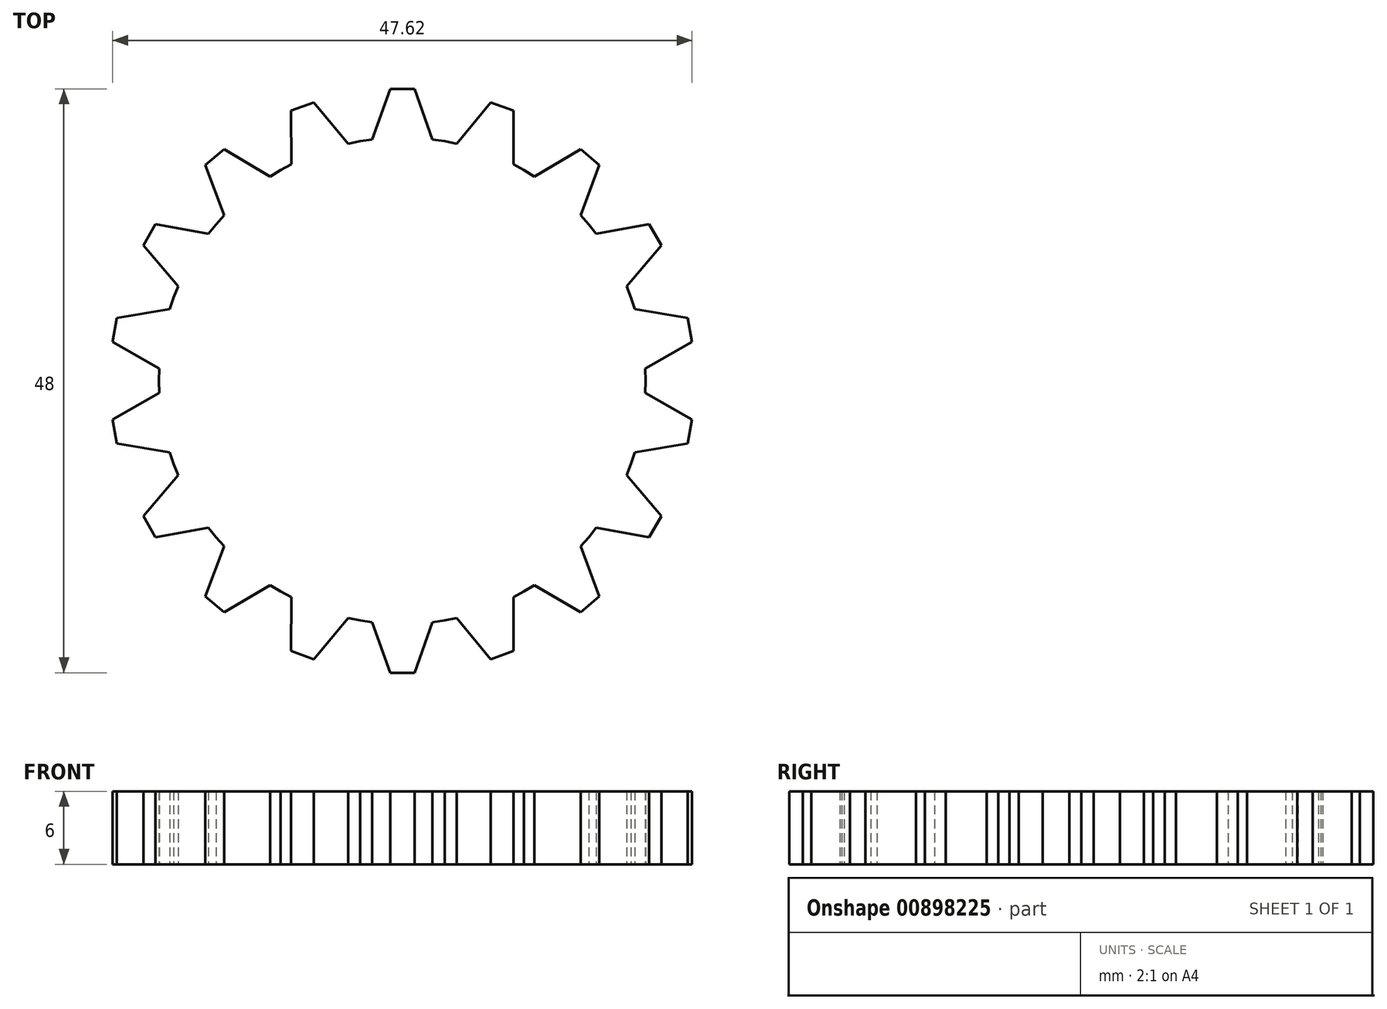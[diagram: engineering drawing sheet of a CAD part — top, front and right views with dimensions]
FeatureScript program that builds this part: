
annotation { "Feature Type Name" : "Feature", "Feature Type Description" : "" }
export const myFeature = defineFeature(function(context is Context, id is Id, definition is map)
    precondition{}
    {
        {
            var Q0;
            Q0=qCreatedBy(makeId("Top.planeOp"),FACE);
            var sketch = newSketch(context, id + "F0", { "sketchPlane" : qUnion([Q0])});
            skCircle(sketch, "E0", {"center": v(0, 0) * mm, "radius": 20 * mm});
            skLineSegment(sketch, "E1", {"start": v(0, 0) * mm, "end": v(-6.59, 37.35) * mm});
            skLineSegment(sketch, "E2", {"start": v(0, 24) * mm, "end": v(-1, 24) * mm});
            skLineSegment(sketch, "E3", {"start": v(-1, 24) * mm, "end": v(-2.48, 19.85) * mm});
            skLineSegment(sketch, "E4", {"start": v(-2.48, 19.85) * mm, "end": v(-3.47, 19.7) * mm});
            skLineSegment(sketch, "E5.MirrorCS", {"start": v(0, 24) * mm, "end": v(1, 24) * mm});
            skLineSegment(sketch, "E6.MirrorCS", {"start": v(2.48, 19.85) * mm, "end": v(3.47, 19.7) * mm});
            skLineSegment(sketch, "E7.MirrorCS", {"start": v(1, 24) * mm, "end": v(2.48, 19.85) * mm});
            skLineSegment(sketch, "E8.1.0", {"start": v(-7.27, 22.9) * mm, "end": v(-4.45, 19.5) * mm});
            skLineSegment(sketch, "E8.1.1", {"start": v(-9.15, 22.21) * mm, "end": v(-9.12, 17.8) * mm});
            skLineSegment(sketch, "E8.1.2", {"start": v(-8.2, 22.55) * mm, "end": v(-7.27, 22.9) * mm});
            skLineSegment(sketch, "E8.1.3", {"start": v(-4.45, 19.5) * mm, "end": v(-3.47, 19.7) * mm});
            skLineSegment(sketch, "E8.1.4", {"start": v(-8.2, 22.55) * mm, "end": v(-9.15, 22.21) * mm});
            skLineSegment(sketch, "E8.1.5", {"start": v(-9.12, 17.8) * mm, "end": v(-10, 17.32) * mm});
            skLineSegment(sketch, "E8.2.0", {"start": v(-14.66, 19.03) * mm, "end": v(-10.85, 16.8) * mm});
            skLineSegment(sketch, "E8.2.1", {"start": v(-16.2, 17.74) * mm, "end": v(-14.66, 13.6) * mm});
            skLineSegment(sketch, "E8.2.2", {"start": v(-15.43, 18.39) * mm, "end": v(-14.66, 19.03) * mm});
            skLineSegment(sketch, "E8.2.3", {"start": v(-10.85, 16.8) * mm, "end": v(-10, 17.32) * mm});
            skLineSegment(sketch, "E8.2.4", {"start": v(-15.43, 18.39) * mm, "end": v(-16.2, 17.74) * mm});
            skLineSegment(sketch, "E8.2.5", {"start": v(-14.66, 13.6) * mm, "end": v(-15.32, 12.86) * mm});
            skLineSegment(sketch, "E8.3.0", {"start": v(-20.28, 12.87) * mm, "end": v(-15.94, 12.07) * mm});
            skLineSegment(sketch, "E8.3.1", {"start": v(-21.28, 11.13) * mm, "end": v(-18.43, 7.77) * mm});
            skLineSegment(sketch, "E8.3.2", {"start": v(-20.78, 12) * mm, "end": v(-20.28, 12.87) * mm});
            skLineSegment(sketch, "E8.3.3", {"start": v(-15.94, 12.07) * mm, "end": v(-15.32, 12.86) * mm});
            skLineSegment(sketch, "E8.3.4", {"start": v(-20.78, 12) * mm, "end": v(-21.28, 11.13) * mm});
            skLineSegment(sketch, "E8.3.5", {"start": v(-18.43, 7.77) * mm, "end": v(-18.8, 6.84) * mm});
            skLineSegment(sketch, "E8.4.0", {"start": v(-23.46, 5.15) * mm, "end": v(-19.11, 5.9) * mm});
            skLineSegment(sketch, "E8.4.1", {"start": v(-23.8, 3.18) * mm, "end": v(-19.98, 1) * mm});
            skLineSegment(sketch, "E8.4.2", {"start": v(-23.64, 4.17) * mm, "end": v(-23.46, 5.15) * mm});
            skLineSegment(sketch, "E8.4.3", {"start": v(-19.11, 5.9) * mm, "end": v(-18.8, 6.84) * mm});
            skLineSegment(sketch, "E8.4.4", {"start": v(-23.64, 4.17) * mm, "end": v(-23.8, 3.18) * mm});
            skLineSegment(sketch, "E8.4.5", {"start": v(-19.98, 1) * mm, "end": v(-20, 0) * mm});
            skLineSegment(sketch, "E8.5.0", {"start": v(-23.8, -3.18) * mm, "end": v(-19.98, -1) * mm});
            skLineSegment(sketch, "E8.5.1", {"start": v(-23.46, -5.15) * mm, "end": v(-19.11, -5.9) * mm});
            skLineSegment(sketch, "E8.5.2", {"start": v(-23.64, -4.17) * mm, "end": v(-23.8, -3.18) * mm});
            skLineSegment(sketch, "E8.5.3", {"start": v(-19.98, -1) * mm, "end": v(-20, 0) * mm});
            skLineSegment(sketch, "E8.5.4", {"start": v(-23.64, -4.17) * mm, "end": v(-23.46, -5.15) * mm});
            skLineSegment(sketch, "E8.5.5", {"start": v(-19.11, -5.9) * mm, "end": v(-18.8, -6.84) * mm});
            skLineSegment(sketch, "E8.6.0", {"start": v(-21.28, -11.13) * mm, "end": v(-18.43, -7.77) * mm});
            skLineSegment(sketch, "E8.6.1", {"start": v(-20.28, -12.87) * mm, "end": v(-15.94, -12.07) * mm});
            skLineSegment(sketch, "E8.6.2", {"start": v(-20.78, -12) * mm, "end": v(-21.28, -11.13) * mm});
            skLineSegment(sketch, "E8.6.3", {"start": v(-18.43, -7.77) * mm, "end": v(-18.8, -6.84) * mm});
            skLineSegment(sketch, "E8.6.4", {"start": v(-20.78, -12) * mm, "end": v(-20.28, -12.87) * mm});
            skLineSegment(sketch, "E8.6.5", {"start": v(-15.94, -12.07) * mm, "end": v(-15.32, -12.86) * mm});
            skLineSegment(sketch, "E8.7.0", {"start": v(-16.2, -17.74) * mm, "end": v(-14.66, -13.6) * mm});
            skLineSegment(sketch, "E8.7.1", {"start": v(-14.66, -19.03) * mm, "end": v(-10.85, -16.8) * mm});
            skLineSegment(sketch, "E8.7.2", {"start": v(-15.43, -18.39) * mm, "end": v(-16.2, -17.74) * mm});
            skLineSegment(sketch, "E8.7.3", {"start": v(-14.66, -13.6) * mm, "end": v(-15.32, -12.86) * mm});
            skLineSegment(sketch, "E8.7.4", {"start": v(-15.43, -18.39) * mm, "end": v(-14.66, -19.03) * mm});
            skLineSegment(sketch, "E8.7.5", {"start": v(-10.85, -16.8) * mm, "end": v(-10, -17.32) * mm});
            skLineSegment(sketch, "E8.8.0", {"start": v(-9.15, -22.21) * mm, "end": v(-9.12, -17.8) * mm});
            skLineSegment(sketch, "E8.8.1", {"start": v(-7.27, -22.9) * mm, "end": v(-4.45, -19.5) * mm});
            skLineSegment(sketch, "E8.8.2", {"start": v(-8.2, -22.55) * mm, "end": v(-9.15, -22.21) * mm});
            skLineSegment(sketch, "E8.8.3", {"start": v(-9.12, -17.8) * mm, "end": v(-10, -17.32) * mm});
            skLineSegment(sketch, "E8.8.4", {"start": v(-8.2, -22.55) * mm, "end": v(-7.27, -22.9) * mm});
            skLineSegment(sketch, "E8.8.5", {"start": v(-4.45, -19.5) * mm, "end": v(-3.47, -19.7) * mm});
            skLineSegment(sketch, "E8.9.0", {"start": v(-1, -24) * mm, "end": v(-2.48, -19.85) * mm});
            skLineSegment(sketch, "E8.9.1", {"start": v(1, -24) * mm, "end": v(2.48, -19.85) * mm});
            skLineSegment(sketch, "E8.9.2", {"start": v(0, -24) * mm, "end": v(-1, -24) * mm});
            skLineSegment(sketch, "E8.9.3", {"start": v(-2.48, -19.85) * mm, "end": v(-3.47, -19.7) * mm});
            skLineSegment(sketch, "E8.9.4", {"start": v(0, -24) * mm, "end": v(1, -24) * mm});
            skLineSegment(sketch, "E8.9.5", {"start": v(2.48, -19.85) * mm, "end": v(3.47, -19.7) * mm});
            skLineSegment(sketch, "E8.10.0", {"start": v(7.27, -22.9) * mm, "end": v(4.45, -19.5) * mm});
            skLineSegment(sketch, "E8.10.1", {"start": v(9.15, -22.21) * mm, "end": v(9.12, -17.8) * mm});
            skLineSegment(sketch, "E8.10.2", {"start": v(8.2, -22.55) * mm, "end": v(7.27, -22.9) * mm});
            skLineSegment(sketch, "E8.10.3", {"start": v(4.45, -19.5) * mm, "end": v(3.47, -19.7) * mm});
            skLineSegment(sketch, "E8.10.4", {"start": v(8.2, -22.55) * mm, "end": v(9.15, -22.21) * mm});
            skLineSegment(sketch, "E8.10.5", {"start": v(9.12, -17.8) * mm, "end": v(10, -17.32) * mm});
            skLineSegment(sketch, "E8.11.0", {"start": v(14.66, -19.03) * mm, "end": v(10.85, -16.8) * mm});
            skLineSegment(sketch, "E8.11.1", {"start": v(16.2, -17.74) * mm, "end": v(14.66, -13.6) * mm});
            skLineSegment(sketch, "E8.11.2", {"start": v(15.43, -18.39) * mm, "end": v(14.66, -19.03) * mm});
            skLineSegment(sketch, "E8.11.3", {"start": v(10.85, -16.8) * mm, "end": v(10, -17.32) * mm});
            skLineSegment(sketch, "E8.11.4", {"start": v(15.43, -18.39) * mm, "end": v(16.2, -17.74) * mm});
            skLineSegment(sketch, "E8.11.5", {"start": v(14.66, -13.6) * mm, "end": v(15.32, -12.86) * mm});
            skLineSegment(sketch, "E8.12.0", {"start": v(20.28, -12.87) * mm, "end": v(15.94, -12.07) * mm});
            skLineSegment(sketch, "E8.12.1", {"start": v(21.28, -11.13) * mm, "end": v(18.43, -7.77) * mm});
            skLineSegment(sketch, "E8.12.2", {"start": v(20.78, -12) * mm, "end": v(20.28, -12.87) * mm});
            skLineSegment(sketch, "E8.12.3", {"start": v(15.94, -12.07) * mm, "end": v(15.32, -12.86) * mm});
            skLineSegment(sketch, "E8.12.4", {"start": v(20.78, -12) * mm, "end": v(21.28, -11.13) * mm});
            skLineSegment(sketch, "E8.12.5", {"start": v(18.43, -7.77) * mm, "end": v(18.8, -6.84) * mm});
            skLineSegment(sketch, "E8.13.0", {"start": v(23.46, -5.15) * mm, "end": v(19.11, -5.9) * mm});
            skLineSegment(sketch, "E8.13.1", {"start": v(23.8, -3.18) * mm, "end": v(19.98, -1) * mm});
            skLineSegment(sketch, "E8.13.2", {"start": v(23.64, -4.17) * mm, "end": v(23.46, -5.15) * mm});
            skLineSegment(sketch, "E8.13.3", {"start": v(19.11, -5.9) * mm, "end": v(18.8, -6.84) * mm});
            skLineSegment(sketch, "E8.13.4", {"start": v(23.64, -4.17) * mm, "end": v(23.8, -3.18) * mm});
            skLineSegment(sketch, "E8.13.5", {"start": v(19.98, -1) * mm, "end": v(20, 0) * mm});
            skLineSegment(sketch, "E8.14.0", {"start": v(23.8, 3.18) * mm, "end": v(19.98, 1) * mm});
            skLineSegment(sketch, "E8.14.1", {"start": v(23.46, 5.15) * mm, "end": v(19.11, 5.9) * mm});
            skLineSegment(sketch, "E8.14.2", {"start": v(23.64, 4.17) * mm, "end": v(23.8, 3.18) * mm});
            skLineSegment(sketch, "E8.14.3", {"start": v(19.98, 1) * mm, "end": v(20, 0) * mm});
            skLineSegment(sketch, "E8.14.4", {"start": v(23.64, 4.17) * mm, "end": v(23.46, 5.15) * mm});
            skLineSegment(sketch, "E8.14.5", {"start": v(19.11, 5.9) * mm, "end": v(18.8, 6.84) * mm});
            skLineSegment(sketch, "E8.15.0", {"start": v(21.28, 11.13) * mm, "end": v(18.43, 7.77) * mm});
            skLineSegment(sketch, "E8.15.1", {"start": v(20.28, 12.87) * mm, "end": v(15.94, 12.07) * mm});
            skLineSegment(sketch, "E8.15.2", {"start": v(20.78, 12) * mm, "end": v(21.28, 11.13) * mm});
            skLineSegment(sketch, "E8.15.3", {"start": v(18.43, 7.77) * mm, "end": v(18.8, 6.84) * mm});
            skLineSegment(sketch, "E8.15.4", {"start": v(20.78, 12) * mm, "end": v(20.28, 12.87) * mm});
            skLineSegment(sketch, "E8.15.5", {"start": v(15.94, 12.07) * mm, "end": v(15.32, 12.86) * mm});
            skLineSegment(sketch, "E8.16.0", {"start": v(16.2, 17.74) * mm, "end": v(14.66, 13.6) * mm});
            skLineSegment(sketch, "E8.16.1", {"start": v(14.66, 19.03) * mm, "end": v(10.85, 16.8) * mm});
            skLineSegment(sketch, "E8.16.2", {"start": v(15.43, 18.39) * mm, "end": v(16.2, 17.74) * mm});
            skLineSegment(sketch, "E8.16.3", {"start": v(14.66, 13.6) * mm, "end": v(15.32, 12.86) * mm});
            skLineSegment(sketch, "E8.16.4", {"start": v(15.43, 18.39) * mm, "end": v(14.66, 19.03) * mm});
            skLineSegment(sketch, "E8.16.5", {"start": v(10.85, 16.8) * mm, "end": v(10, 17.32) * mm});
            skLineSegment(sketch, "E8.17.0", {"start": v(9.15, 22.21) * mm, "end": v(9.12, 17.8) * mm});
            skLineSegment(sketch, "E8.17.1", {"start": v(7.27, 22.9) * mm, "end": v(4.45, 19.5) * mm});
            skLineSegment(sketch, "E8.17.2", {"start": v(8.2, 22.55) * mm, "end": v(9.15, 22.21) * mm});
            skLineSegment(sketch, "E8.17.3", {"start": v(9.12, 17.8) * mm, "end": v(10, 17.32) * mm});
            skLineSegment(sketch, "E8.17.4", {"start": v(8.2, 22.55) * mm, "end": v(7.27, 22.9) * mm});
            skLineSegment(sketch, "E8.17.5", {"start": v(4.45, 19.5) * mm, "end": v(3.47, 19.7) * mm});
            skSolve(sketch);
        }
        {
            var Q0;
            {var subQ1=sQuery(id+"F0.wireOp",EDGE,"2a4dd31f-a686-42c0-beec-bc84213fc3c1.2.0");Q0=makeQuery(id+"F0.imprint","IMPRINT",FACE,{"disambiguationData":[TD([[makeQuery(id+"F0.imprint","IMPRINT",EDGE,{"derivedFrom":subQ1}),1.0]])]});}
            var Q1;
            {var subQ21=sQuery(id+"F0.wireOp",EDGE,"E4");Q1=makeQuery(id+"F0.imprint","IMPRINT",FACE,{"disambiguationData":[TD([[makeQuery(id+"F0.imprint","IMPRINT",EDGE,{"derivedFrom":subQ21}),1.0]])]});}
            var Q2;
            {var subQ0=sQuery(id+"F0.wireOp",EDGE,"2a4dd31f-a686-42c0-beec-bc84213fc3c1.1.0");Q2=makeQuery(id+"F0.imprint","IMPRINT",FACE,{"disambiguationData":[TD([[makeQuery(id+"F0.imprint","IMPRINT",EDGE,{"derivedFrom":subQ0}),1.0]])]});}
            var Q3;
            Q3=makeQuery(id+"F0.imprint","IMPRINT",FACE,{"disambiguationData":[TD([[makeQuery(id+"F0.imprint","IMPRINT",EDGE,{"derivedFrom":sQuery(id+"F0.wireOp",EDGE,"E2")}),1.0]])]});
            var Q4;
            {var subQ1=sQuery(id+"F0.wireOp",EDGE,"2a4dd31f-a686-42c0-beec-bc84213fc3c1.16.0");Q4=makeQuery(id+"F0.imprint","IMPRINT",FACE,{"disambiguationData":[TD([[makeQuery(id+"F0.imprint","IMPRINT",EDGE,{"derivedFrom":subQ1}),1.0]])]});}
            var Q5;
            {var subQ0=sQuery(id+"F0.wireOp",EDGE,"2a4dd31f-a686-42c0-beec-bc84213fc3c1.15.0");Q5=makeQuery(id+"F0.imprint","IMPRINT",FACE,{"disambiguationData":[TD([[makeQuery(id+"F0.imprint","IMPRINT",EDGE,{"derivedFrom":subQ0}),1.0]])]});}
            var Q6;
            {var subQ1=sQuery(id+"F0.wireOp",EDGE,"2a4dd31f-a686-42c0-beec-bc84213fc3c1.17.0");Q6=makeQuery(id+"F0.imprint","IMPRINT",FACE,{"disambiguationData":[TD([[makeQuery(id+"F0.imprint","IMPRINT",EDGE,{"derivedFrom":subQ1}),1.0]])]});}
            var Q7;
            {var subQ1=sQuery(id+"F0.wireOp",EDGE,"2a4dd31f-a686-42c0-beec-bc84213fc3c1.13.0");Q7=makeQuery(id+"F0.imprint","IMPRINT",FACE,{"disambiguationData":[TD([[makeQuery(id+"F0.imprint","IMPRINT",EDGE,{"derivedFrom":subQ1}),1.0]])]});}
            var Q8;
            {var subQ1=sQuery(id+"F0.wireOp",EDGE,"2a4dd31f-a686-42c0-beec-bc84213fc3c1.12.0");Q8=makeQuery(id+"F0.imprint","IMPRINT",FACE,{"disambiguationData":[TD([[makeQuery(id+"F0.imprint","IMPRINT",EDGE,{"derivedFrom":subQ1}),1.0]])]});}
            var Q9;
            {var subQ1=sQuery(id+"F0.wireOp",EDGE,"2a4dd31f-a686-42c0-beec-bc84213fc3c1.14.0");Q9=makeQuery(id+"F0.imprint","IMPRINT",FACE,{"disambiguationData":[TD([[makeQuery(id+"F0.imprint","IMPRINT",EDGE,{"derivedFrom":subQ1}),1.0]])]});}
            var Q10;
            {var subQ0=sQuery(id+"F0.wireOp",EDGE,"2a4dd31f-a686-42c0-beec-bc84213fc3c1.11.0");Q10=makeQuery(id+"F0.imprint","IMPRINT",FACE,{"disambiguationData":[TD([[makeQuery(id+"F0.imprint","IMPRINT",EDGE,{"derivedFrom":subQ0}),1.0]])]});}
            var Q11;
            {var subQ1=sQuery(id+"F0.wireOp",EDGE,"2a4dd31f-a686-42c0-beec-bc84213fc3c1.10.0");Q11=makeQuery(id+"F0.imprint","IMPRINT",FACE,{"disambiguationData":[TD([[makeQuery(id+"F0.imprint","IMPRINT",EDGE,{"derivedFrom":subQ1}),1.0]])]});}
            var Q12;
            {var subQ1=sQuery(id+"F0.wireOp",EDGE,"2a4dd31f-a686-42c0-beec-bc84213fc3c1.9.0");Q12=makeQuery(id+"F0.imprint","IMPRINT",FACE,{"disambiguationData":[TD([[makeQuery(id+"F0.imprint","IMPRINT",EDGE,{"derivedFrom":subQ1}),1.0]])]});}
            var Q13;
            {var subQ1=sQuery(id+"F0.wireOp",EDGE,"2a4dd31f-a686-42c0-beec-bc84213fc3c1.8.0");Q13=makeQuery(id+"F0.imprint","IMPRINT",FACE,{"disambiguationData":[TD([[makeQuery(id+"F0.imprint","IMPRINT",EDGE,{"derivedFrom":subQ1}),1.0]])]});}
            var Q14;
            {var subQ1=sQuery(id+"F0.wireOp",EDGE,"2a4dd31f-a686-42c0-beec-bc84213fc3c1.7.0");Q14=makeQuery(id+"F0.imprint","IMPRINT",FACE,{"disambiguationData":[TD([[makeQuery(id+"F0.imprint","IMPRINT",EDGE,{"derivedFrom":subQ1}),1.0]])]});}
            var Q15;
            {var subQ0=sQuery(id+"F0.wireOp",EDGE,"2a4dd31f-a686-42c0-beec-bc84213fc3c1.6.0");Q15=makeQuery(id+"F0.imprint","IMPRINT",FACE,{"disambiguationData":[TD([[makeQuery(id+"F0.imprint","IMPRINT",EDGE,{"derivedFrom":subQ0}),1.0]])]});}
            var Q16;
            {var subQ1=sQuery(id+"F0.wireOp",EDGE,"2a4dd31f-a686-42c0-beec-bc84213fc3c1.5.0");Q16=makeQuery(id+"F0.imprint","IMPRINT",FACE,{"disambiguationData":[TD([[makeQuery(id+"F0.imprint","IMPRINT",EDGE,{"derivedFrom":subQ1}),1.0]])]});}
            var Q17;
            {var subQ1=sQuery(id+"F0.wireOp",EDGE,"2a4dd31f-a686-42c0-beec-bc84213fc3c1.4.0");Q17=makeQuery(id+"F0.imprint","IMPRINT",FACE,{"disambiguationData":[TD([[makeQuery(id+"F0.imprint","IMPRINT",EDGE,{"derivedFrom":subQ1}),1.0]])]});}
            var Q18;
            {var subQ1=sQuery(id+"F0.wireOp",EDGE,"2a4dd31f-a686-42c0-beec-bc84213fc3c1.3.0");Q18=makeQuery(id+"F0.imprint","IMPRINT",FACE,{"disambiguationData":[TD([[makeQuery(id+"F0.imprint","IMPRINT",EDGE,{"derivedFrom":subQ1}),1.0]])]});}
            var Q19;
            {var subQ1=sQuery(id+"F0.wireOp",EDGE,"E8.17.0");Q19=makeQuery(id+"F0.imprint","IMPRINT",FACE,{"disambiguationData":[TD([[makeQuery(id+"F0.imprint","IMPRINT",EDGE,{"derivedFrom":subQ1}),-1.0]])]});}
            var Q20;
            {var subQ1=sQuery(id+"F0.wireOp",EDGE,"E8.16.0");Q20=makeQuery(id+"F0.imprint","IMPRINT",FACE,{"disambiguationData":[TD([[makeQuery(id+"F0.imprint","IMPRINT",EDGE,{"derivedFrom":subQ1}),-1.0]])]});}
            var Q21;
            {var subQ1=sQuery(id+"F0.wireOp",EDGE,"E8.15.0");Q21=makeQuery(id+"F0.imprint","IMPRINT",FACE,{"disambiguationData":[TD([[makeQuery(id+"F0.imprint","IMPRINT",EDGE,{"derivedFrom":subQ1}),-1.0]])]});}
            var Q22;
            {var subQ1=sQuery(id+"F0.wireOp",EDGE,"E8.14.0");Q22=makeQuery(id+"F0.imprint","IMPRINT",FACE,{"disambiguationData":[TD([[makeQuery(id+"F0.imprint","IMPRINT",EDGE,{"derivedFrom":subQ1}),-1.0]])]});}
            var Q23;
            {var subQ1=sQuery(id+"F0.wireOp",EDGE,"E8.13.0");Q23=makeQuery(id+"F0.imprint","IMPRINT",FACE,{"disambiguationData":[TD([[makeQuery(id+"F0.imprint","IMPRINT",EDGE,{"derivedFrom":subQ1}),-1.0]])]});}
            var Q24;
            {var subQ1=sQuery(id+"F0.wireOp",EDGE,"E8.12.0");Q24=makeQuery(id+"F0.imprint","IMPRINT",FACE,{"disambiguationData":[TD([[makeQuery(id+"F0.imprint","IMPRINT",EDGE,{"derivedFrom":subQ1}),-1.0]])]});}
            var Q25;
            {var subQ0=sQuery(id+"F0.wireOp",EDGE,"E8.11.0");Q25=makeQuery(id+"F0.imprint","IMPRINT",FACE,{"disambiguationData":[TD([[makeQuery(id+"F0.imprint","IMPRINT",EDGE,{"derivedFrom":subQ0}),-1.0]])]});}
            var Q26;
            {var subQ1=sQuery(id+"F0.wireOp",EDGE,"E8.10.0");Q26=makeQuery(id+"F0.imprint","IMPRINT",FACE,{"disambiguationData":[TD([[makeQuery(id+"F0.imprint","IMPRINT",EDGE,{"derivedFrom":subQ1}),-1.0]])]});}
            var Q27;
            {var subQ1=sQuery(id+"F0.wireOp",EDGE,"E8.9.0");Q27=makeQuery(id+"F0.imprint","IMPRINT",FACE,{"disambiguationData":[TD([[makeQuery(id+"F0.imprint","IMPRINT",EDGE,{"derivedFrom":subQ1}),-1.0]])]});}
            var Q28;
            {var subQ1=sQuery(id+"F0.wireOp",EDGE,"E8.8.0");Q28=makeQuery(id+"F0.imprint","IMPRINT",FACE,{"disambiguationData":[TD([[makeQuery(id+"F0.imprint","IMPRINT",EDGE,{"derivedFrom":subQ1}),-1.0]])]});}
            var Q29;
            {var subQ1=sQuery(id+"F0.wireOp",EDGE,"E8.7.0");Q29=makeQuery(id+"F0.imprint","IMPRINT",FACE,{"disambiguationData":[TD([[makeQuery(id+"F0.imprint","IMPRINT",EDGE,{"derivedFrom":subQ1}),-1.0]])]});}
            var Q30;
            {var subQ0=sQuery(id+"F0.wireOp",EDGE,"E8.6.0");Q30=makeQuery(id+"F0.imprint","IMPRINT",FACE,{"disambiguationData":[TD([[makeQuery(id+"F0.imprint","IMPRINT",EDGE,{"derivedFrom":subQ0}),-1.0]])]});}
            var Q31;
            {var subQ1=sQuery(id+"F0.wireOp",EDGE,"E8.5.0");Q31=makeQuery(id+"F0.imprint","IMPRINT",FACE,{"disambiguationData":[TD([[makeQuery(id+"F0.imprint","IMPRINT",EDGE,{"derivedFrom":subQ1}),-1.0]])]});}
            var Q32;
            {var subQ1=sQuery(id+"F0.wireOp",EDGE,"E8.4.0");Q32=makeQuery(id+"F0.imprint","IMPRINT",FACE,{"disambiguationData":[TD([[makeQuery(id+"F0.imprint","IMPRINT",EDGE,{"derivedFrom":subQ1}),-1.0]])]});}
            var Q33;
            {var subQ1=sQuery(id+"F0.wireOp",EDGE,"E8.3.0");Q33=makeQuery(id+"F0.imprint","IMPRINT",FACE,{"disambiguationData":[TD([[makeQuery(id+"F0.imprint","IMPRINT",EDGE,{"derivedFrom":subQ1}),-1.0]])]});}
            var Q34;
            {var subQ1=sQuery(id+"F0.wireOp",EDGE,"E8.2.0");Q34=makeQuery(id+"F0.imprint","IMPRINT",FACE,{"disambiguationData":[TD([[makeQuery(id+"F0.imprint","IMPRINT",EDGE,{"derivedFrom":subQ1}),-1.0]])]});}
            var Q35;
            {var subQ0=sQuery(id+"F0.wireOp",EDGE,"E8.1.0");Q35=makeQuery(id+"F0.imprint","IMPRINT",FACE,{"disambiguationData":[TD([[makeQuery(id+"F0.imprint","IMPRINT",EDGE,{"derivedFrom":subQ0}),-1.0]])]});}
            extrude(context, id + "F1", {"entities" : qUnion([Q0, Q1, Q2, Q3, Q4, Q5, Q6, Q7, Q8, Q9, Q10, Q11, Q12, Q13, Q14, Q15, Q16, Q17, Q18, Q19, Q20, Q21, Q22, Q23, Q24, Q25, Q26, Q27, Q28, Q29, Q30, Q31, Q32, Q33, Q34, Q35]), "depth" : 6 * mm, "offsetDistance" : 25 * mm});
        }
    });
